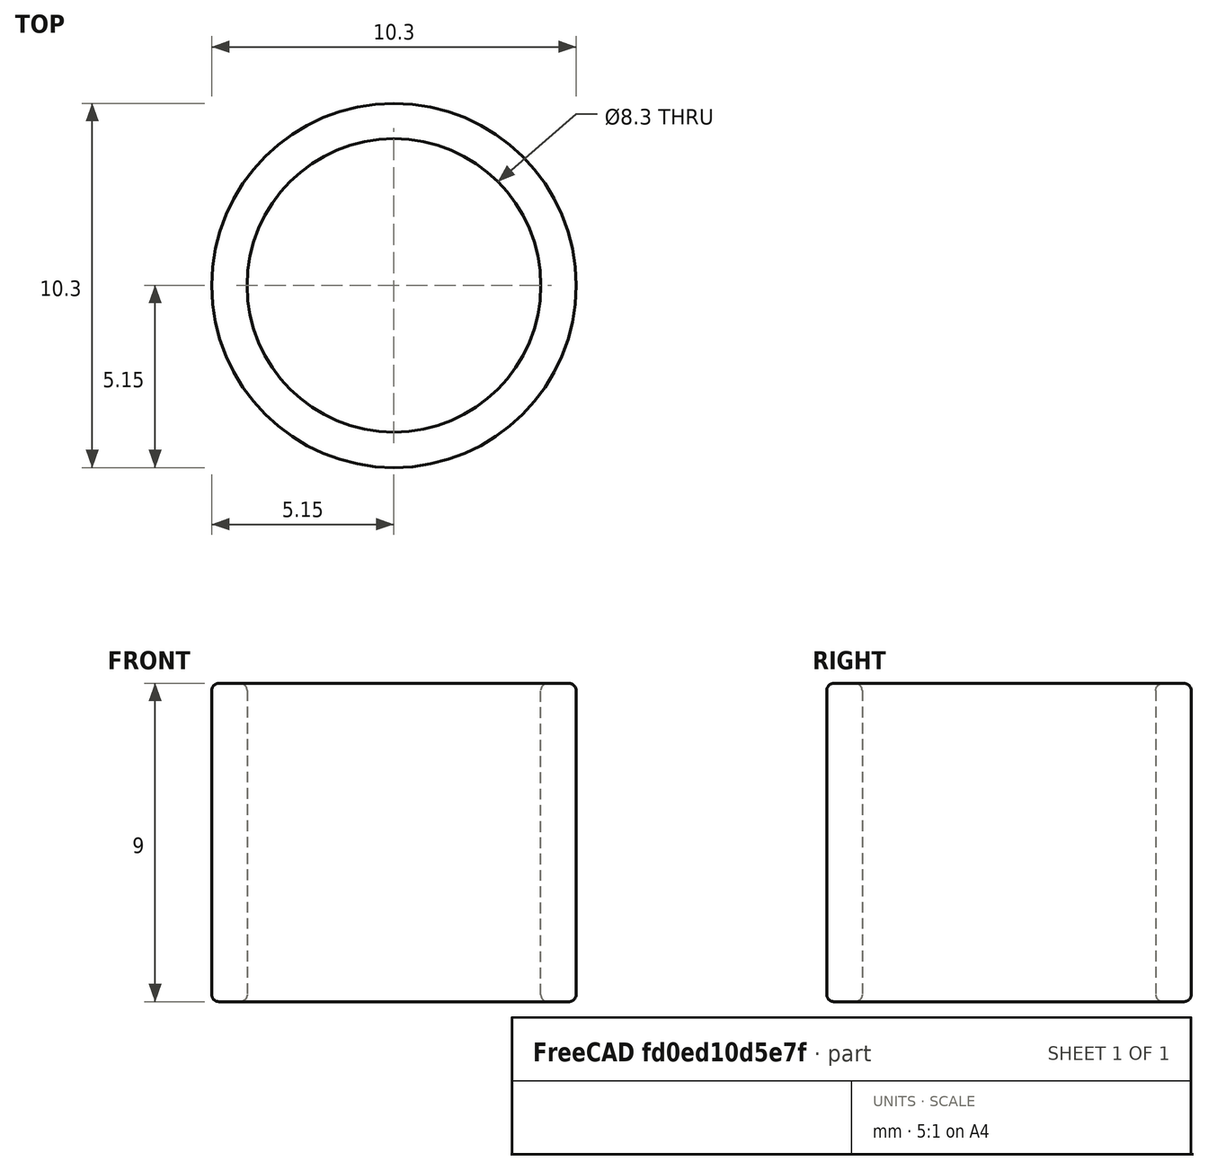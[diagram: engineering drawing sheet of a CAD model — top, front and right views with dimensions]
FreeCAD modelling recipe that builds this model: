
FCSTD DOCUMENT  (FreeCAD 0.21R33694 (Git))
Label: Tube V 8.3 int Tete Plate
License: All rights reserved
LicenseURL: http://en.wikipedia.org/wiki/All_rights_reserved
objects: PartDesign::Fillet×2, Sketcher::SketchObject×1, PartDesign::Pad×1, PartDesign::Body×1
note: 8 computed .brp shape members not serialized (recipe doc carries the construction recipe); baked Part::Feature solids carry a one-line shape summary decoded from their .brp

FEATURE [Sketcher::SketchObject] Sketch
  FullyConstrained = false
  MapMode = 5
  Support = -> [XY_Plane]
  sketch-geometry (2):
    g0: Circle CenterX=0 CenterY=0 CenterZ=0 NormalX=0 NormalY=0 NormalZ=1 AngleXU=0 Radius=4.15
    g1: Circle CenterX=0 CenterY=0 CenterZ=0 NormalX=0 NormalY=0 NormalZ=1 AngleXU=0 Radius=5.15
  constraints (2):
    c: Diameter(g0) = 8.3
    c: Diameter(g1) = 10.3
FEATURE [PartDesign::Pad] Pad
  AllowMultiFace = false
  Direction = (0,0,1)
  Length = 9
  Length2 = 100
  Profile = -> Sketch
  Type = 0
FEATURE [PartDesign::Fillet] Fillet
  Base = -> Pad [Face4]
  BaseFeature = -> Pad
  Radius = 0.2
  Refine = true
  SupportTransform = false
  UseAllEdges = false
FEATURE [PartDesign::Fillet] Fillet001
  Base = -> Fillet [Face3]
  BaseFeature = -> Fillet
  Radius = 0.2
  Refine = true
  SupportTransform = false
  UseAllEdges = false
FEATURE [PartDesign::Body] Body
  Group = -> [Sketch,Pad,Fillet,Fillet001]
  Origin = -> Origin
  Tip = -> Fillet001
